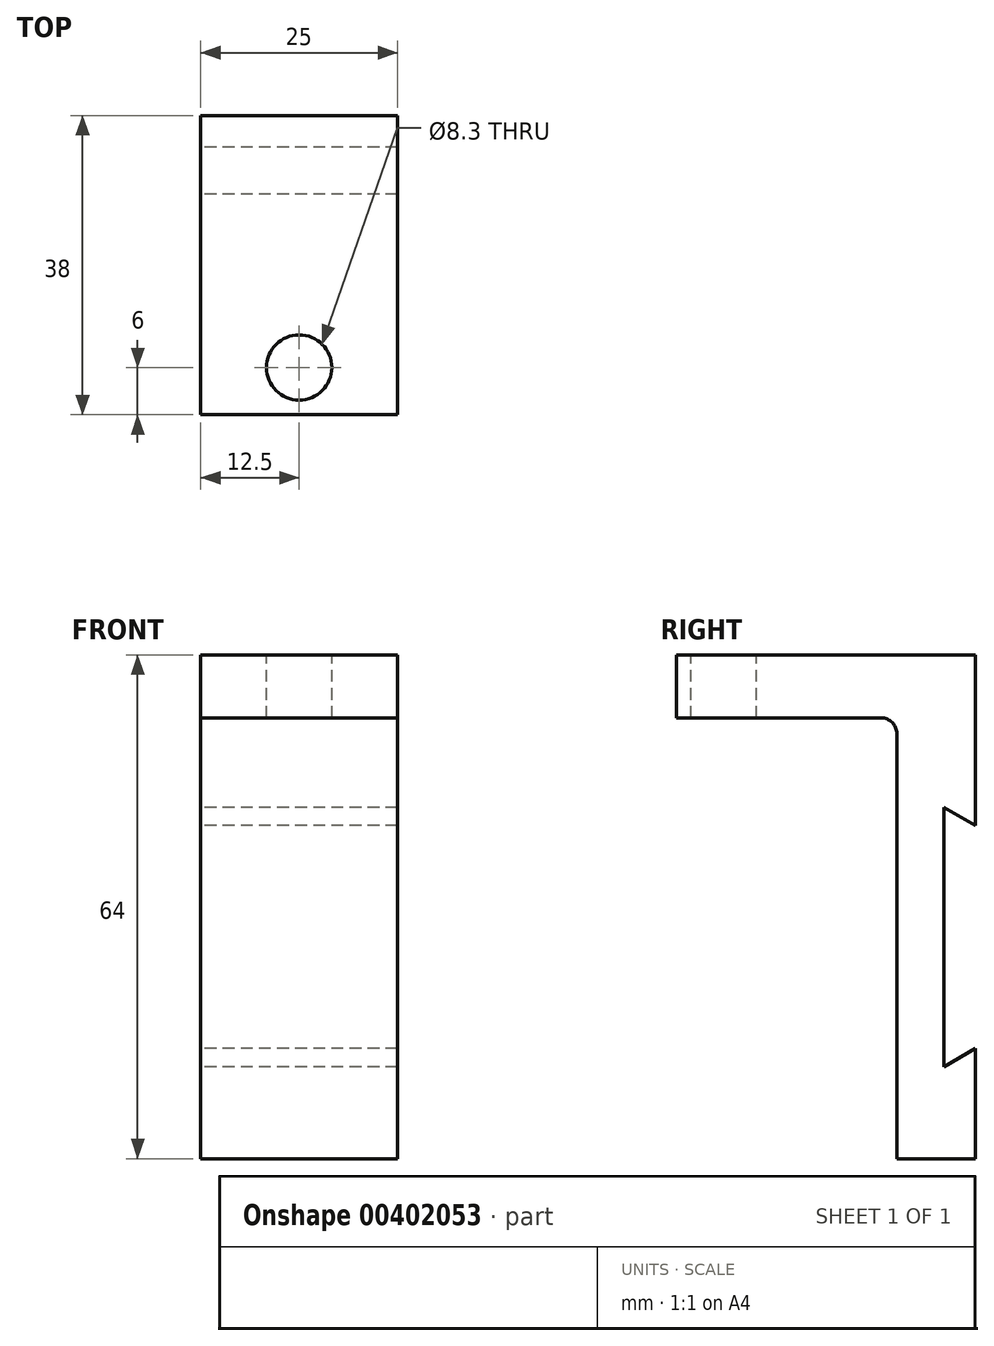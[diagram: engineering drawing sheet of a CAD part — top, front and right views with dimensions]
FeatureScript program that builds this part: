
annotation { "Feature Type Name" : "Feature", "Feature Type Description" : "" }
export const myFeature = defineFeature(function(context is Context, id is Id, definition is map)
    precondition{}
    {
        {
            var Q0;
            Q0=qCreatedBy(makeId("Right.planeOp"),FACE);
            var sketch = newSketch(context, id + "F0", { "sketchPlane" : qUnion([Q0])});
            skLineSegment(sketch, "E0", {"start": v(0, 20.6) * mm, "end": v(0, -12.3) * mm});
            skLineSegment(sketch, "E1", {"start": v(0, -12.3) * mm, "end": v(4, -10) * mm});
            skLineSegment(sketch, "E2", {"start": v(4, -10) * mm, "end": v(4, -24) * mm});
            skLineSegment(sketch, "E3", {"start": v(4, -24) * mm, "end": v(-6, -24) * mm});
            skLineSegment(sketch, "E4", {"start": v(-6, -24) * mm, "end": v(-6, 32) * mm});
            skLineSegment(sketch, "E5", {"start": v(-6, 40) * mm, "end": v(4, 40) * mm});
            skLineSegment(sketch, "E6", {"start": v(4, 40) * mm, "end": v(4, 18.3) * mm});
            skLineSegment(sketch, "E7", {"start": v(4, 18.3) * mm, "end": v(0, 20.6) * mm});
            skLineSegment(sketch, "E8", {"start": v(-6, 32) * mm, "end": v(-34, 32) * mm});
            skLineSegment(sketch, "E9", {"start": v(-34, 32) * mm, "end": v(-34, 40) * mm});
            skLineSegment(sketch, "E10", {"start": v(-34, 40) * mm, "end": v(-6, 40) * mm});
            skSolve(sketch);
        }
        {
            var Q0;
            Q0 = qSketchRegion(id + "F0", true);
            extrude(context, id + "F1", {"entities" : qUnion([Q0]), "endBound" : BoundingType.SYMMETRIC, "depth" : 25 * mm});
        }
        {
            var Q0;
            Q0=makeQuery(id+"F1.opExtrude","SWEPT_FACE",FACE,{"disambiguationData":[OSD([sQuery(id+"F0.wireOp",EDGE,"E5"),sQuery(id+"F0.wireOp",EDGE,"E10")])]});
            var sketch = newSketch(context, id + "F2", { "sketchPlane" : qUnion([Q0])});
            skCircle(sketch, "E11", {"center": v(0, -28) * mm, "radius": 4.15 * mm});
            skSolve(sketch);
        }
        {
            var Q0;
            Q0 = qSketchRegion(id + "F2", true);
            extrude(context, id + "F3", {"entities" : qUnion([Q0]), "operationType" : NewBodyOperationType.REMOVE, "endBound" : BoundingType.UP_TO_NEXT, "oppositeDirection" : true, "depth" : 25 * mm});
        }
        {
            var Q0;
            Q0=makeQuery(id+"F1.opExtrude","SWEPT_EDGE",EDGE,{"disambiguationData":[OSD([sQuery(id+"F0.wireOp",EDGE,"E4"),sQuery(id+"F0.wireOp",EDGE,"E8")])]});
            fillet(context, id + "F4", {"entities" : qUnion([Q0]), "radius" : 2 * mm, "tangentPropagation" : true, "allowEdgeOverflow" : false});
        }
    });
